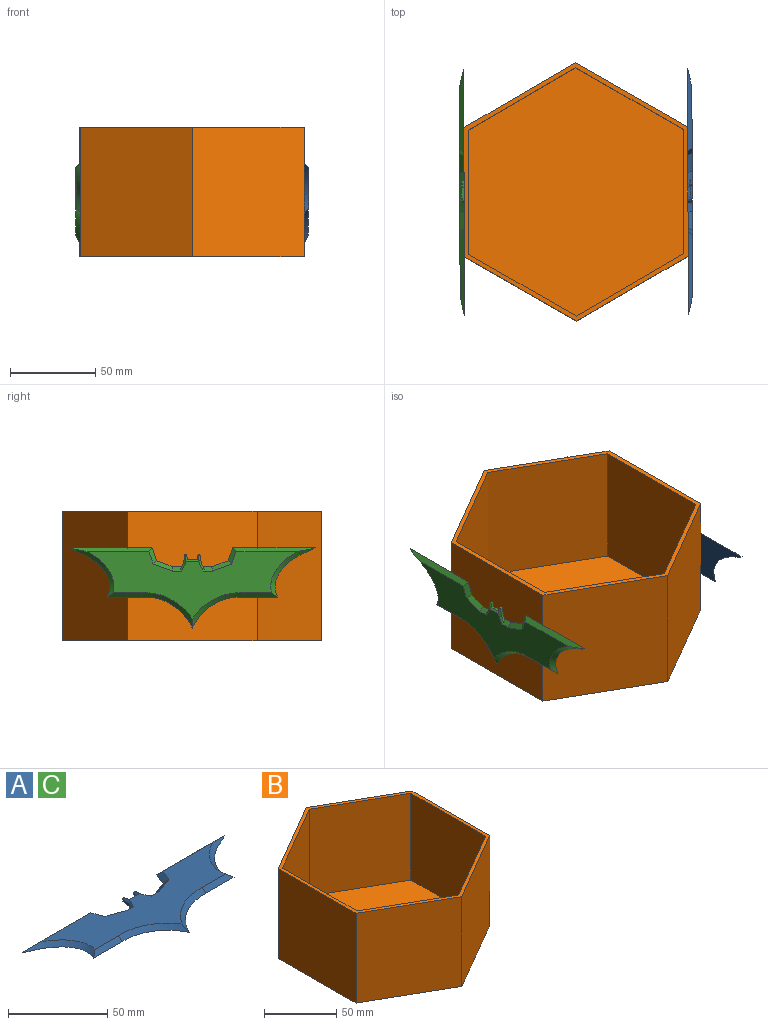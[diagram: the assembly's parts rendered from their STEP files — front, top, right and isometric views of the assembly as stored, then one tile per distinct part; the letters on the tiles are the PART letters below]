
ASSEMBLY  parts=3 mates=2
PART A: 32 faces, bbox 150.6x54.5x6.9 mm
  f0: plane 3.32x1.82mm, normal (-0.88,0.48,0), area 4.4mm2, adj f1,f6,f8,f31
  f1: plane 5.43x1.52mm, normal (-0.99,0.16,0), area 8.4mm2, adj f0,f2,f6,f30
  f2: plane 2.01x0.98mm, normal (0,1,0), area 1.7mm2, adj f1,f3,f6,f29,f30
  f3: plane 2.99x1.52mm, normal (0.98,0.19,0), area 4.6mm2, adj f2,f4,f6,f29
  f4: plane 5.67x1.52mm, normal (0,1,0), area 8.6mm2, adj f3,f6,f17,f28
  f5: plane 122.93x39.76mm, normal (0,0,1), area 2233.1mm2, adj f7,f8,f9,f10,f11,f12,f13,f18
  f6: plane 148.73x51.77mm, normal (0,0,-1), area 3052.8mm2, adj f0,f1,f2,f3,f4,f7,f8,f9
  f7: cone r=31.04mm half-angle=45deg, axis (0,0,1), area 130.9mm2, adj f5,f6,f9,f18
  f8: plane 5.54x2.54mm, normal (0,0.71,0.71), area 17.4mm2, adj f0,f5,f6,f10,f31
  f9: plane 20.74x3.18mm, normal (0,-0.71,0.71), area 65.6mm2, adj f5,f6,f7,f11
  f10: plane 11.73x6.12mm, normal (0.24,0.66,0.71), area 40.2mm2, adj f5,f6,f8,f12
  f11: bspline ~34.79x27.08mm, area 127.5mm2, adj f5,f6,f9,f13
  f12: plane 9.68x4.5mm, normal (0.67,0.23,0.71), area 28.2mm2, adj f5,f6,f10,f13
  f13: plane 49.77x3.89mm, normal (0,0.71,0.71), area 152.5mm2, adj f5,f6,f11,f12
  f14: plane 3.32x1.82mm, normal (0.88,0.48,0), area 4.4mm2, adj f6,f15,f19,f25
  f15: plane 5.43x1.52mm, normal (0.99,0.16,0), area 8.4mm2, adj f6,f14,f16,f26
  f16: plane 2.01x0.98mm, normal (0,1,0), area 1.7mm2, adj f6,f15,f17,f26,f27
  f17: plane 2.99x1.52mm, normal (-0.98,0.19,0), area 4.6mm2, adj f4,f6,f16,f27
  f18: cone r=31.04mm half-angle=45deg, axis (0,0,1), area 130.9mm2, adj f5,f6,f7,f20
  f19: plane 5.54x2.54mm, normal (0,0.71,0.71), area 17.4mm2, adj f5,f6,f14,f21,f25
  f20: plane 20.74x3.18mm, normal (0,-0.71,0.71), area 65.6mm2, adj f5,f6,f18,f22
  f21: plane 11.73x6.12mm, normal (-0.24,0.66,0.71), area 40.2mm2, adj f5,f6,f19,f23
  f22: bspline ~34.79x27.08mm, area 127.5mm2, adj f5,f6,f20,f24
  f23: plane 9.68x4.5mm, normal (-0.67,0.23,0.71), area 28.2mm2, adj f5,f6,f21,f24
  f24: plane 49.77x3.89mm, normal (0,0.71,0.71), area 152.5mm2, adj f5,f6,f22,f23
  f25: plane 4.33x2.79mm, normal (0.62,0.34,0.71), area 6mm2, adj f5,f14,f19,f26
  f26: plane 5.76x1.41mm, normal (0.7,0.11,0.71), area 7mm2, adj f5,f15,f16,f25,f27
  f27: plane 4x1.06mm, normal (-0.69,0.13,0.71), area 3.9mm2, adj f5,f16,f17,f26,f28
  f28: plane 7.35x1.02mm, normal (0,0.71,0.71), area 9.4mm2, adj f4,f5,f27,f29
  f29: plane 4x1.06mm, normal (0.69,0.13,0.71), area 3.9mm2, adj f2,f3,f5,f28,f30
  f30: plane 5.76x1.41mm, normal (-0.7,0.11,0.71), area 7mm2, adj f1,f2,f5,f29,f31
  f31: plane 4.33x2.79mm, normal (-0.62,0.34,0.71), area 6mm2, adj f0,f5,f8,f30
PART B: 15 faces, bbox 131.8x151.9x76.2 mm
  f0: plane 151.93x131.84mm, normal (0,0,1), area 1135.4mm2, adj f1,f2,f3,f4,f5,f6,f8,f9
  f1: plane 76.2x75.97mm, normal (1,0,0), area 5788.7mm2, adj f0,f2,f6,f7
  f2: plane 76.2x65.92mm, normal (0.5,0.87,0), area 5788.7mm2, adj f0,f1,f3,f7
  f3: plane 76.2x65.66mm, normal (-0.5,0.86,0), area 5788.7mm2, adj f0,f2,f4,f7
  f4: plane 76.2x75.97mm, normal (-1,0,0), area 5788.7mm2, adj f0,f3,f5,f7
  f5: plane 76.2x65.92mm, normal (-0.5,-0.87,0), area 5788.7mm2, adj f0,f4,f6,f7
  f6: plane 76.2x65.66mm, normal (0.5,-0.86,0), area 5788.7mm2, adj f0,f1,f5,f7
  f7: plane 151.93x131.84mm, normal (0,0,-1), area 14993.6mm2, adj f1,f2,f3,f4,f5,f6
  f8: plane 73.66x73.03mm, normal (-1,0,0), area 5379.7mm2, adj f0,f9,f13,f14
  f9: plane 73.66x63.38mm, normal (-0.5,-0.87,0), area 5379.7mm2, adj f0,f8,f10,f14
  f10: plane 73.66x63.12mm, normal (0.5,-0.86,0), area 5379.7mm2, adj f0,f9,f11,f14
  f11: plane 73.66x73.03mm, normal (1,0,0), area 5379.7mm2, adj f0,f10,f12,f14
  f12: plane 73.66x63.38mm, normal (0.5,0.87,0), area 5379.7mm2, adj f0,f11,f13,f14
  f13: plane 73.66x63.12mm, normal (-0.5,0.86,0), area 5379.7mm2, adj f0,f8,f12,f14
  f14: plane 146.07x126.75mm, normal (0,0,1), area 13858.2mm2, adj f8,f9,f10,f11,f12,f13
PART C: same geometry as A
PLACE A rot(axis=(0.58,0.58,0.58),120.1deg) t=(57.1,54.05,16.27)mm
PLACE B t=(-8.68,53.82,-12.78)mm
PLACE C rot(axis=(0.58,-0.58,-0.58),119.9deg) t=(-74.47,53.59,16.27)mm
MATE fastened A.f6 <-> B.f1  axis (-1,0,0) through (57.1,54.05,25.32)mm
MATE fastened C.f6 <-> B.f4  axis (1,0,0) through (-74.47,53.59,25.32)mm
